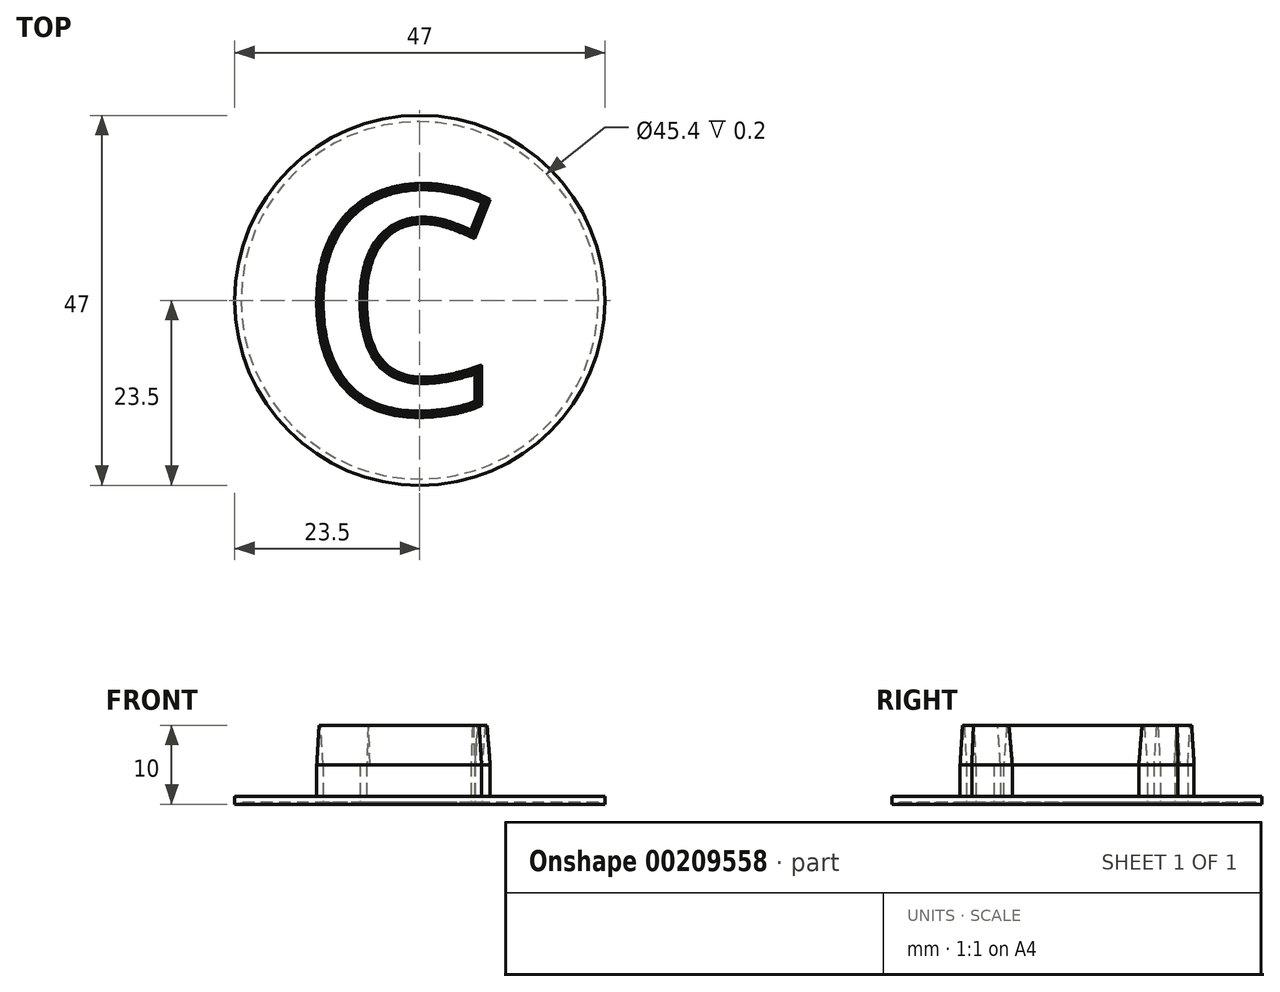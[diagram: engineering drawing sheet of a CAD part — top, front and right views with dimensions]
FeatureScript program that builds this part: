
annotation { "Feature Type Name" : "Feature", "Feature Type Description" : "" }
export const myFeature = defineFeature(function(context is Context, id is Id, definition is map)
    precondition{}
    {
        {
            var Q0;
            Q0=qCreatedBy(makeId("Top.planeOp"),FACE);
            var sketch = newSketch(context, id + "F0", { "sketchPlane" : qUnion([Q0])});
            skCircle(sketch, "E0", {"center": v(0, 0) * mm, "radius": 23.5 * mm});
            skText(sketch, "E1", { "text": "C", "fontName": "OpenSans-Bold.ttf"});
            const initialGuessF0  = {"E1": [-0.01544, -0.01446, 1, 0, 0.02915]};
            skSetInitialGuess(sketch, initialGuessF0);
            skSolve(sketch);
        }
        {
            var Q0;
            Q0=makeQuery(id+"F0.imprint","IMPRINT",FACE,{"disambiguationData":[TD([[makeQuery(id+"F0.imprint","IMPRINT",EDGE,{"derivedFrom":sQuery(id+"F0.wireOp",EDGE,"E0")}),1.0]])]});
            extrude(context, id + "F1", {"entities" : qUnion([Q0]), "depth" : 1 * mm});
        }
        {
            var Q0;
            Q0=makeQuery(id+"F0.imprint","IMPRINT",FACE,{"disambiguationData":[TD([[makeQuery(id+"F0.imprint","IMPRINT",EDGE,{"derivedFrom":sQuery(id+"F0.wireOp",EDGE,"E1.sketch_text.stroke-0")}),-1.0]])]});
            extrude(context, id + "F2", {"entities" : qUnion([Q0]), "operationType" : NewBodyOperationType.ADD, "depth" : 10 * mm});
        }
        {
            var Q0;
            Q0=makeQuery(id+"F2.opExtrude","CAP_FACE",FACE,{"disambiguationData":[OSD([sQuery(id+"F0.wireOp",EDGE,"E1.sketch_text.stroke-0"),sQuery(id+"F0.wireOp",EDGE,"E1.sketch_text.stroke-1"),sQuery(id+"F0.wireOp",EDGE,"E1.sketch_text.stroke-2"),sQuery(id+"F0.wireOp",EDGE,"E1.sketch_text.stroke-3"),sQuery(id+"F0.wireOp",EDGE,"E1.sketch_text.stroke-4"),sQuery(id+"F0.wireOp",EDGE,"E1.sketch_text.stroke-5"),sQuery(id+"F0.wireOp",EDGE,"E1.sketch_text.stroke-6"),sQuery(id+"F0.wireOp",EDGE,"E1.sketch_text.stroke-7"),sQuery(id+"F0.wireOp",EDGE,"E1.sketch_text.stroke-8"),sQuery(id+"F0.wireOp",EDGE,"E1.sketch_text.stroke-9"),sQuery(id+"F0.wireOp",EDGE,"E1.sketch_text.stroke-10"),sQuery(id+"F0.wireOp",EDGE,"E1.sketch_text.stroke-11"),sQuery(id+"F0.wireOp",EDGE,"E1.sketch_text.stroke-12"),sQuery(id+"F0.wireOp",EDGE,"E1.sketch_text.stroke-13"),sQuery(id+"F0.wireOp",EDGE,"E1.sketch_text.stroke-14")])],"isStart":false});
            var Q1;
            Q1=makeQuery(id+"F2.opExtrude","CAP_FACE",FACE,{"disambiguationData":[OSD([sQuery(id+"F0.wireOp",EDGE,"E1.sketch_text.stroke-0"),sQuery(id+"F0.wireOp",EDGE,"E1.sketch_text.stroke-1"),sQuery(id+"F0.wireOp",EDGE,"E1.sketch_text.stroke-2"),sQuery(id+"F0.wireOp",EDGE,"E1.sketch_text.stroke-3"),sQuery(id+"F0.wireOp",EDGE,"E1.sketch_text.stroke-4"),sQuery(id+"F0.wireOp",EDGE,"E1.sketch_text.stroke-5"),sQuery(id+"F0.wireOp",EDGE,"E1.sketch_text.stroke-6"),sQuery(id+"F0.wireOp",EDGE,"E1.sketch_text.stroke-7"),sQuery(id+"F0.wireOp",EDGE,"E1.sketch_text.stroke-8"),sQuery(id+"F0.wireOp",EDGE,"E1.sketch_text.stroke-9"),sQuery(id+"F0.wireOp",EDGE,"E1.sketch_text.stroke-10"),sQuery(id+"F0.wireOp",EDGE,"E1.sketch_text.stroke-11"),sQuery(id+"F0.wireOp",EDGE,"E1.sketch_text.stroke-12"),sQuery(id+"F0.wireOp",EDGE,"E1.sketch_text.stroke-13"),sQuery(id+"F0.wireOp",EDGE,"E1.sketch_text.stroke-14")])],"isStart":true});
            shell(context, id + "F3", {"entities" : qUnion([Q0, Q1]), "thickness" : 0.8 * mm});
        }
        {
            var Q0;
            Q0=makeQuery(id+"F2.opExtrude","CAP_FACE",FACE,{"disambiguationData":[OSD([sQuery(id+"F0.wireOp",EDGE,"E1.sketch_text.stroke-0"),sQuery(id+"F0.wireOp",EDGE,"E1.sketch_text.stroke-1"),sQuery(id+"F0.wireOp",EDGE,"E1.sketch_text.stroke-2"),sQuery(id+"F0.wireOp",EDGE,"E1.sketch_text.stroke-3"),sQuery(id+"F0.wireOp",EDGE,"E1.sketch_text.stroke-4"),sQuery(id+"F0.wireOp",EDGE,"E1.sketch_text.stroke-5"),sQuery(id+"F0.wireOp",EDGE,"E1.sketch_text.stroke-6"),sQuery(id+"F0.wireOp",EDGE,"E1.sketch_text.stroke-7"),sQuery(id+"F0.wireOp",EDGE,"E1.sketch_text.stroke-8"),sQuery(id+"F0.wireOp",EDGE,"E1.sketch_text.stroke-9"),sQuery(id+"F0.wireOp",EDGE,"E1.sketch_text.stroke-10"),sQuery(id+"F0.wireOp",EDGE,"E1.sketch_text.stroke-11"),sQuery(id+"F0.wireOp",EDGE,"E1.sketch_text.stroke-12"),sQuery(id+"F0.wireOp",EDGE,"E1.sketch_text.stroke-13"),sQuery(id+"F0.wireOp",EDGE,"E1.sketch_text.stroke-14")])],"isStart":false});
            chamfer(context, id + "F4", {"entities" : qUnion([Q0]), "chamferType" : ChamferType.TWO_OFFSETS, "width1" : 0.3 * mm, "oppositeDirection" : true, "width2" : 5 * mm, "tangentPropagation" : true});
        }
    });
